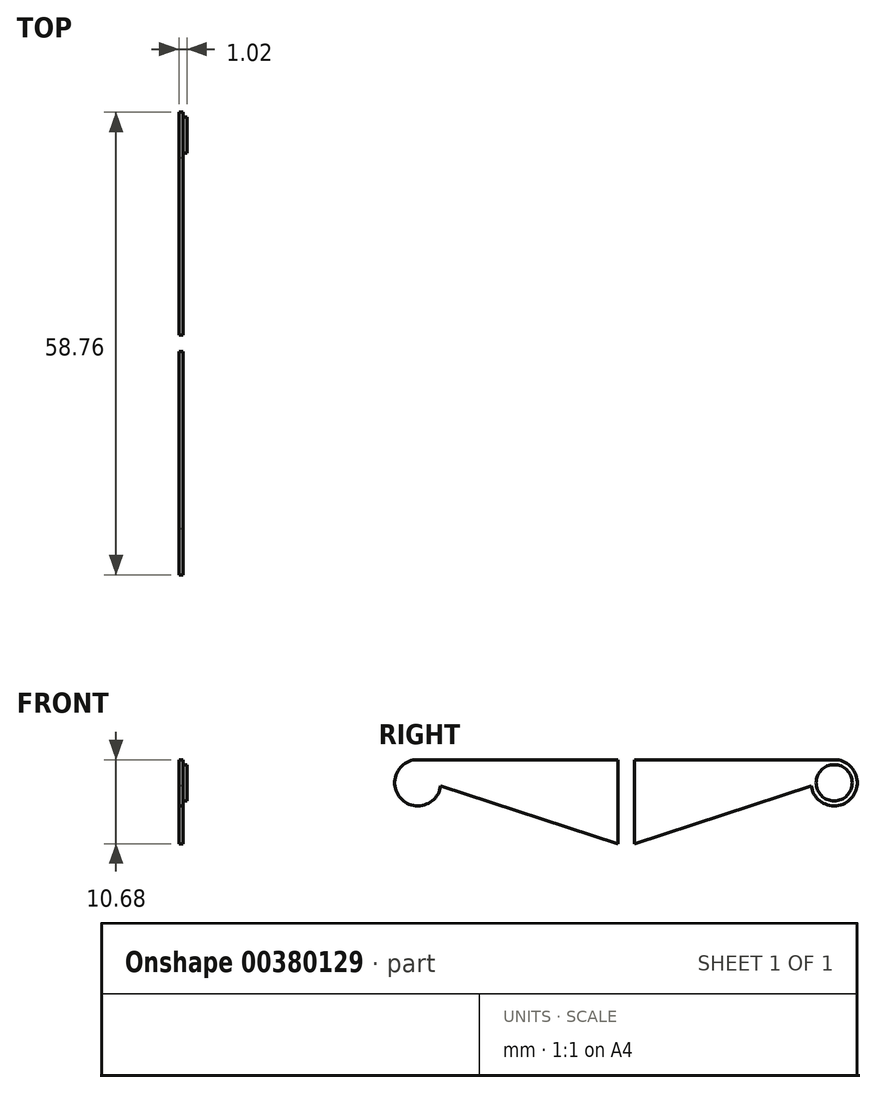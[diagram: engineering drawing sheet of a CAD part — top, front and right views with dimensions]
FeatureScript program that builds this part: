
annotation { "Feature Type Name" : "Feature", "Feature Type Description" : "" }
export const myFeature = defineFeature(function(context is Context, id is Id, definition is map)
    precondition{}
    {
        {
            var Q0;
            Q0=qCreatedBy(makeId("Right.planeOp"),FACE);
            var sketch = newSketch(context, id + "F0", { "sketchPlane" : qUnion([Q0])});
            skLineSegment(sketch, "E0", {"start": v(-13.41, 5.15) * mm, "end": v(-13.41, -5.53) * mm});
            skLineSegment(sketch, "E1", {"start": v(-13.41, 5.15) * mm, "end": v(11.99, 5.15) * mm});
            skLineSegment(sketch, "E2", {"start": v(-13.41, -5.53) * mm, "end": v(9.08, 1.83) * mm});
            skArc(sketch, "E3", {"start": v(11.99, 5.15) * mm, "mid": v(14.2, 0.29) * mm, "end": v(9.08, 1.83) * mm});
            skLineSegment(sketch, "E4", {"start": v(-14.46, 5.15) * mm, "end": v(-14.46, -5.5) * mm});
            skLineSegment(sketch, "E5.MirrorCS", {"start": v(-15.5, 5.15) * mm, "end": v(-15.5, -5.53) * mm});
            skLineSegment(sketch, "E6.MirrorCS", {"start": v(-15.5, 5.15) * mm, "end": v(-40.9, 5.15) * mm});
            skLineSegment(sketch, "E7.MirrorCS", {"start": v(-15.5, -5.53) * mm, "end": v(-38, 1.83) * mm});
            skArc(sketch, "E8.MirrorCS", {"start": v(-40.9, 5.15) * mm, "mid": v(-43.11, 0.29) * mm, "end": v(-38, 1.83) * mm});
            skSolve(sketch);
        }
        {
            var Q0;
            Q0 = qSketchRegion(id + "F0", true);
            extrude(context, id + "F1", {"entities" : qUnion([Q0]), "depth" : 0.5 * mm});
        }
        {
            var Q0;
            Q0=makeQuery(id+"F1.opExtrude","CAP_FACE",FACE,{"disambiguationData":[OSD([sQuery(id+"F0.wireOp",EDGE,"E0"),sQuery(id+"F0.wireOp",EDGE,"E1"),sQuery(id+"F0.wireOp",EDGE,"E2"),sQuery(id+"F0.wireOp",EDGE,"E3")])],"isStart":false});
            var sketch = newSketch(context, id + "F2", { "sketchPlane" : qUnion([Q0])});
            skCircle(sketch, "E9", {"center": v(11.99, 2.22) * mm, "radius": 2.3 * mm});
            skSolve(sketch);
        }
        {
            var Q0;
            Q0=makeQuery(id+"F2.imprint","IMPRINT",FACE,{"disambiguationData":[TD([[makeQuery(id+"F2.imprint","IMPRINT",EDGE,{"derivedFrom":sQuery(id+"F2.wireOp",EDGE,"E9")}),1.0]])]});
            extrude(context, id + "F3", {"entities" : qUnion([Q0]), "depth" : 0.5 * mm});
        }
    });
